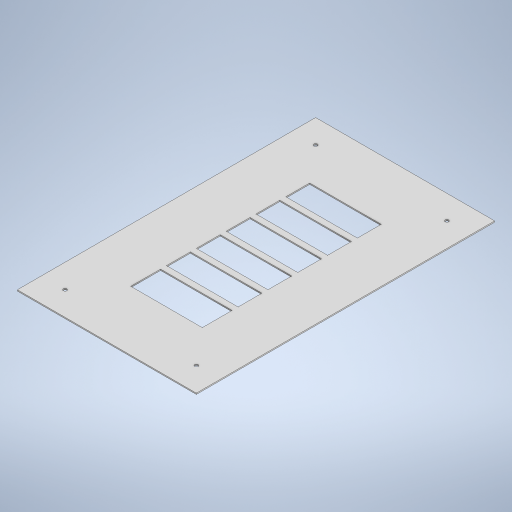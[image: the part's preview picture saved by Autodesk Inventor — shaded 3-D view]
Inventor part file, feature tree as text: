
AUTODESK INVENTOR PART (.ipt)
format: ipt  version: 2024 (Build 280153000, 153)  size: 262,656 bytes
history: native  units: mm
features: other x1, extrude x1, sketch x1
ambient origin geometry x8: Origin, YZ Plane, XZ Plane, XY Plane, X Axis, Y Axis, Z Axis, Center Point
bodies: Body1 (feature_tree)
feature tree (3):
  other  "Sólido1"
  extrude  "Extrusión1"  Depth=60.0mm
  sketch  "Boceto1"  dims[d0=10.0mm d1=60.0mm d2=160.0mm d3=45.0mm d6=50.0mm d7=25.0mm d8=5.0mm d9=60.0mm d11=25.0mm d12=10.0mm d14=10.0mm d16=1.0mm d17=0.0mm]
